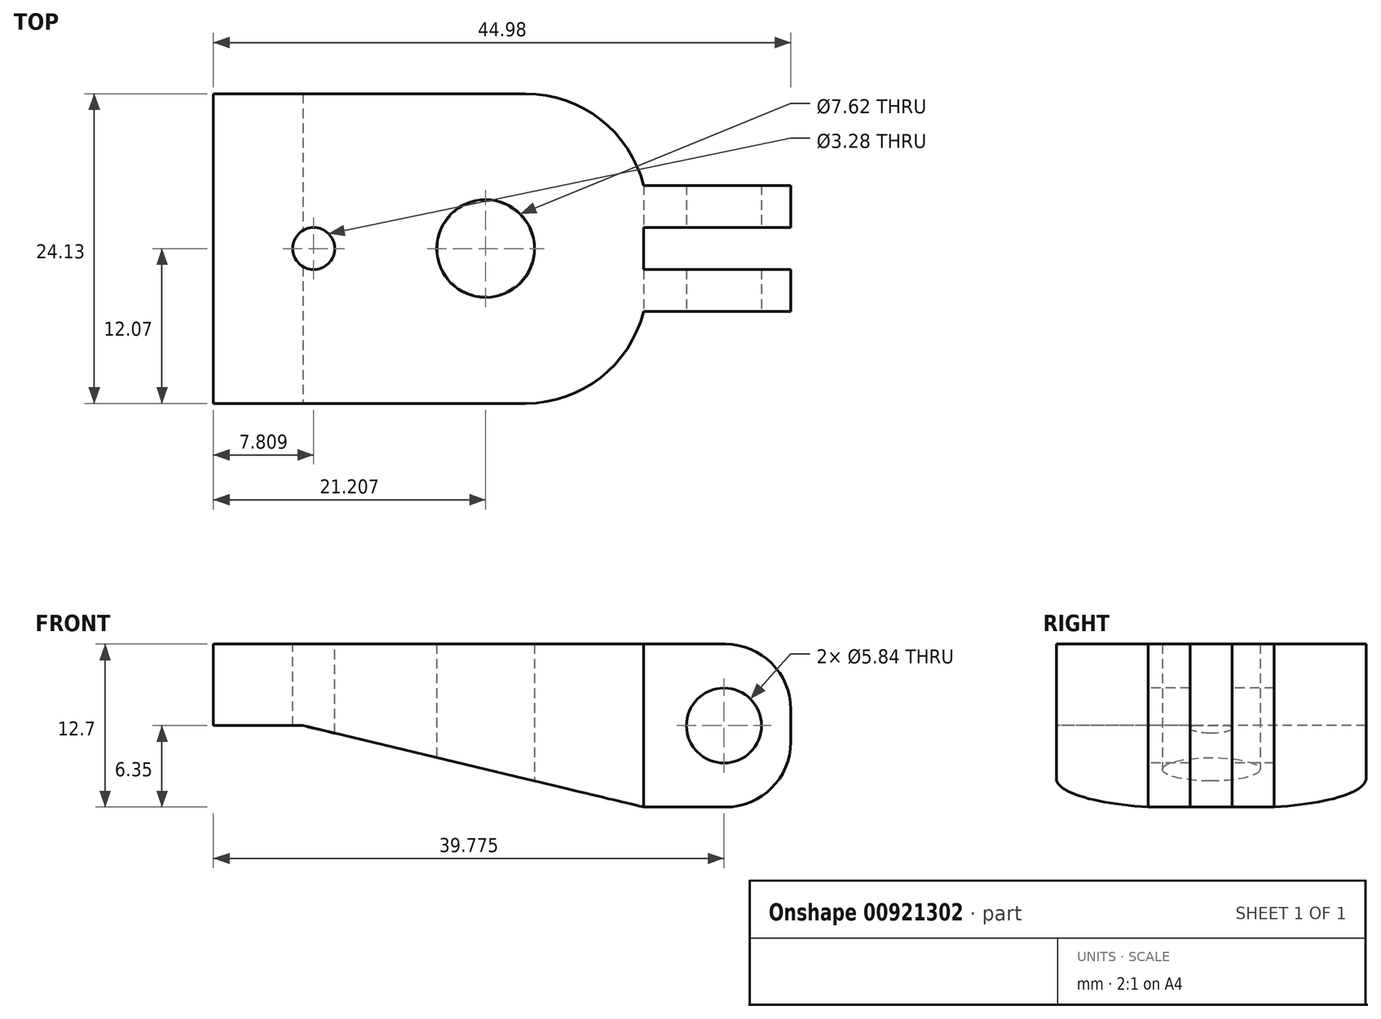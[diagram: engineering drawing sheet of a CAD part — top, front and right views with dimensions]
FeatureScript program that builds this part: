
annotation { "Feature Type Name" : "Feature", "Feature Type Description" : "" }
export const myFeature = defineFeature(function(context is Context, id is Id, definition is map)
    precondition{}
    {
        {
            var Q0;
            Q0=qCreatedBy(makeId("Top.planeOp"),FACE);
            var sketch = newSketch(context, id + "F0", { "sketchPlane" : qUnion([Q0])});
            skLineSegment(sketch, "E0.bottom", {"start": v(-12.94, 12.07) * mm, "end": v(11.38, 12.07) * mm});
            skLineSegment(sketch, "E0.top", {"start": v(-12.94, -12.07) * mm, "end": v(11.38, -12.07) * mm});
            skLineSegment(sketch, "E0.left", {"start": v(-12.94, 12.07) * mm, "end": v(-12.94, -12.07) * mm});
            skLineSegment(sketch, "E0.right", {"start": v(32.04, 4.91) * mm, "end": v(32.04, 1.64) * mm});
            skLineSegment(sketch, "E1", {"start": v(20.57, 1.64) * mm, "end": v(20.57, -1.64) * mm});
            skLineSegment(sketch, "E2.0", {"start": v(20.48, -1.64) * mm, "end": v(32.04, -1.64) * mm});
            skLineSegment(sketch, "E3.0", {"start": v(20.48, 1.64) * mm, "end": v(32.04, 1.64) * mm});
            skLineSegment(sketch, "E4.0", {"start": v(20.57, 4.91) * mm, "end": v(32.04, 4.91) * mm});
            skLineSegment(sketch, "E5.0", {"start": v(20.57, -4.91) * mm, "end": v(32.04, -4.91) * mm});
            skLineSegment(sketch, "E6.trimOffspring", {"start": v(32.04, -1.64) * mm, "end": v(32.04, -4.91) * mm});
            skCircle(sketch, "E7", {"center": v(8.27, 0) * mm, "radius": 3.81 * mm});
            skArc(sketch, "E8", {"start": v(20.57, 4.91) * mm, "mid": v(17.2, 10.07) * mm, "end": v(11.38, 12.07) * mm});
            skArc(sketch, "E9", {"start": v(11.38, -12.07) * mm, "mid": v(17.2, -10.07) * mm, "end": v(20.57, -4.91) * mm});
            skSolve(sketch);
        }
        {
            var Q0;
            Q0=makeQuery(id+"F0.imprint","IMPRINT",FACE,{"disambiguationData":[TD([[makeQuery(id+"F0.imprint","IMPRINT",EDGE,{"derivedFrom":sQuery(id+"F0.wireOp",EDGE,"E0.bottom")}),-1.0]])]});
            var Q1;
            Q1=makeQuery(id+"F0.imprint","IMPRINT",FACE,{"disambiguationData":[TD([[makeQuery(id+"F0.imprint","IMPRINT",EDGE,{"derivedFrom":sQuery(id+"F0.wireOp",EDGE,"E0.right")}),-1.0]])]});
            var Q2;
            {var subQ2=sQuery(id+"F0.wireOp",EDGE,"E2.0");Q2=makeQuery(id+"F0.imprint","IMPRINT",FACE,{"disambiguationData":[TD([[makeQuery(id+"F0.imprint","IMPRINT",EDGE,{"derivedFrom":subQ2}),-1.0]])]});}
            extrude(context, id + "F1", {"entities" : qUnion([Q0, Q1, Q2]), "depth" : 12.7 * mm, "offsetDistance" : 25.4 * mm});
        }
        {
            var Q0;
            Q0=makeQuery(id+"F1.opExtrude","SWEPT_FACE",FACE,{"disambiguationData":[OSD([sQuery(id+"F0.wireOp",EDGE,"E5.0")])]});
            var sketch = newSketch(context, id + "F2", { "sketchPlane" : qUnion([Q0])});
            skCircle(sketch, "E10", {"center": v(26.84, 6.35) * mm, "radius": 2.92 * mm});
            skPoint(sketch, "E10.centerSnap0", {"position": v(20.49, 6.35) * mm});
            skSolve(sketch);
        }
        {
            var Q0;
            Q0=makeQuery(id+"F1.opExtrude","CAP_EDGE",EDGE,{"disambiguationData":[OSD([sQuery(id+"F0.wireOp",EDGE,"E6.trimOffspring")])],"isStart":false});
            var Q1;
            Q1=makeQuery(id+"F1.opExtrude","CAP_EDGE",EDGE,{"disambiguationData":[OSD([sQuery(id+"F0.wireOp",EDGE,"E0.right")])],"isStart":false});
            var Q2;
            Q2=makeQuery(id+"F1.opExtrude","CAP_EDGE",EDGE,{"disambiguationData":[OSD([sQuery(id+"F0.wireOp",EDGE,"E6.trimOffspring")])],"isStart":true});
            var Q3;
            Q3=makeQuery(id+"F1.opExtrude","CAP_EDGE",EDGE,{"disambiguationData":[OSD([sQuery(id+"F0.wireOp",EDGE,"E0.right")])],"isStart":true});
            fillet(context, id + "F3", {"entities" : qUnion([Q0, Q1, Q2, Q3]), "radius" : 5.08 * mm, "tangentPropagation" : true, "allowEdgeOverflow" : false});
        }
        {
            var Q0;
            Q0=makeQuery(id+"F2.imprint","IMPRINT",FACE,{"disambiguationData":[TD([[makeQuery(id+"F2.imprint","IMPRINT",EDGE,{"derivedFrom":sQuery(id+"F2.wireOp",EDGE,"E10")}),1.0]])]});
            extrude(context, id + "F4", {"entities" : qUnion([Q0]), "operationType" : NewBodyOperationType.REMOVE, "endBound" : BoundingType.THROUGH_ALL, "oppositeDirection" : true, "depth" : 25.4 * mm, "offsetDistance" : 25.4 * mm});
        }
        {
            var Q0;
            Q0=makeQuery(id+"F1.opExtrude","SWEPT_FACE",FACE,{"disambiguationData":[OSD([sQuery(id+"F0.wireOp",EDGE,"E0.top")])]});
            var sketch = newSketch(context, id + "F5", { "sketchPlane" : qUnion([Q0])});
            skLineSegment(sketch, "E11", {"start": v(-12.94, 6.35) * mm, "end": v(-5.97, 6.35) * mm});
            skLineSegment(sketch, "E12", {"start": v(-12.94, 0) * mm, "end": v(-12.94, 0) * mm});
            skLineSegment(sketch, "E13", {"start": v(-12.94, 0) * mm, "end": v(-12.94, 6.35) * mm});
            skLineSegment(sketch, "E14", {"start": v(11.38, 0) * mm, "end": v(-12.94, 0) * mm});
            skLineSegment(sketch, "E15", {"start": v(-5.97, 6.35) * mm, "end": v(20.59, 0) * mm});
            skLineSegment(sketch, "E16", {"start": v(20.59, 0) * mm, "end": v(11.38, 0) * mm});
            skSolve(sketch);
        }
        {
            var Q0;
            Q0=makeQuery(id+"F5.imprint","IMPRINT",FACE,{"disambiguationData":[TD([[makeQuery(id+"F5.imprint","IMPRINT",EDGE,{"derivedFrom":sQuery(id+"F5.wireOp",EDGE,"E11")}),-1.0]])]});
            var Q1;
            {var subQ0=sQuery(id+"F5.wireOp",EDGE,"E16");Q1=makeQuery(id+"F5.imprint","IMPRINT",FACE,{"disambiguationData":[TD([[makeQuery(id+"F5.imprint","IMPRINT",EDGE,{"derivedFrom":subQ0}),-1.0]])]});}
            extrude(context, id + "F6", {"entities" : qUnion([Q0, Q1]), "operationType" : NewBodyOperationType.REMOVE, "endBound" : BoundingType.THROUGH_ALL, "oppositeDirection" : true, "depth" : 25.4 * mm, "offsetDistance" : 25.4 * mm});
        }
        {
            var Q0;
            Q0=makeQuery(id+"F1.opExtrude","CAP_FACE",FACE,{"disambiguationData":[OSD([sQuery(id+"F0.wireOp",EDGE,"E0.bottom"),sQuery(id+"F0.wireOp",EDGE,"E0.top"),sQuery(id+"F0.wireOp",EDGE,"E0.left"),sQuery(id+"F0.wireOp",EDGE,"E0.right"),sQuery(id+"F0.wireOp",EDGE,"E1"),sQuery(id+"F0.wireOp",EDGE,"E2.0"),sQuery(id+"F0.wireOp",EDGE,"E3.0"),sQuery(id+"F0.wireOp",EDGE,"E4.0"),sQuery(id+"F0.wireOp",EDGE,"E5.0"),sQuery(id+"F0.wireOp",EDGE,"E6.trimOffspring"),sQuery(id+"F0.wireOp",EDGE,"E7"),sQuery(id+"F0.wireOp",EDGE,"E8"),sQuery(id+"F0.wireOp",EDGE,"E9")])],"isStart":false});
            var sketch = newSketch(context, id + "F7", { "sketchPlane" : qUnion([Q0])});
            skCircle(sketch, "E17", {"center": v(-5.13, 0) * mm, "radius": 1.64 * mm});
            skSolve(sketch);
        }
        {
            var Q0;
            Q0=makeQuery(id+"F7.imprint","IMPRINT",FACE,{"disambiguationData":[TD([[makeQuery(id+"F7.imprint","IMPRINT",EDGE,{"derivedFrom":sQuery(id+"F7.wireOp",EDGE,"E17")}),1.0]])]});
            extrude(context, id + "F8", {"entities" : qUnion([Q0]), "operationType" : NewBodyOperationType.REMOVE, "oppositeDirection" : true, "depth" : 25.4 * mm, "offsetDistance" : 25.4 * mm});
        }
    });
